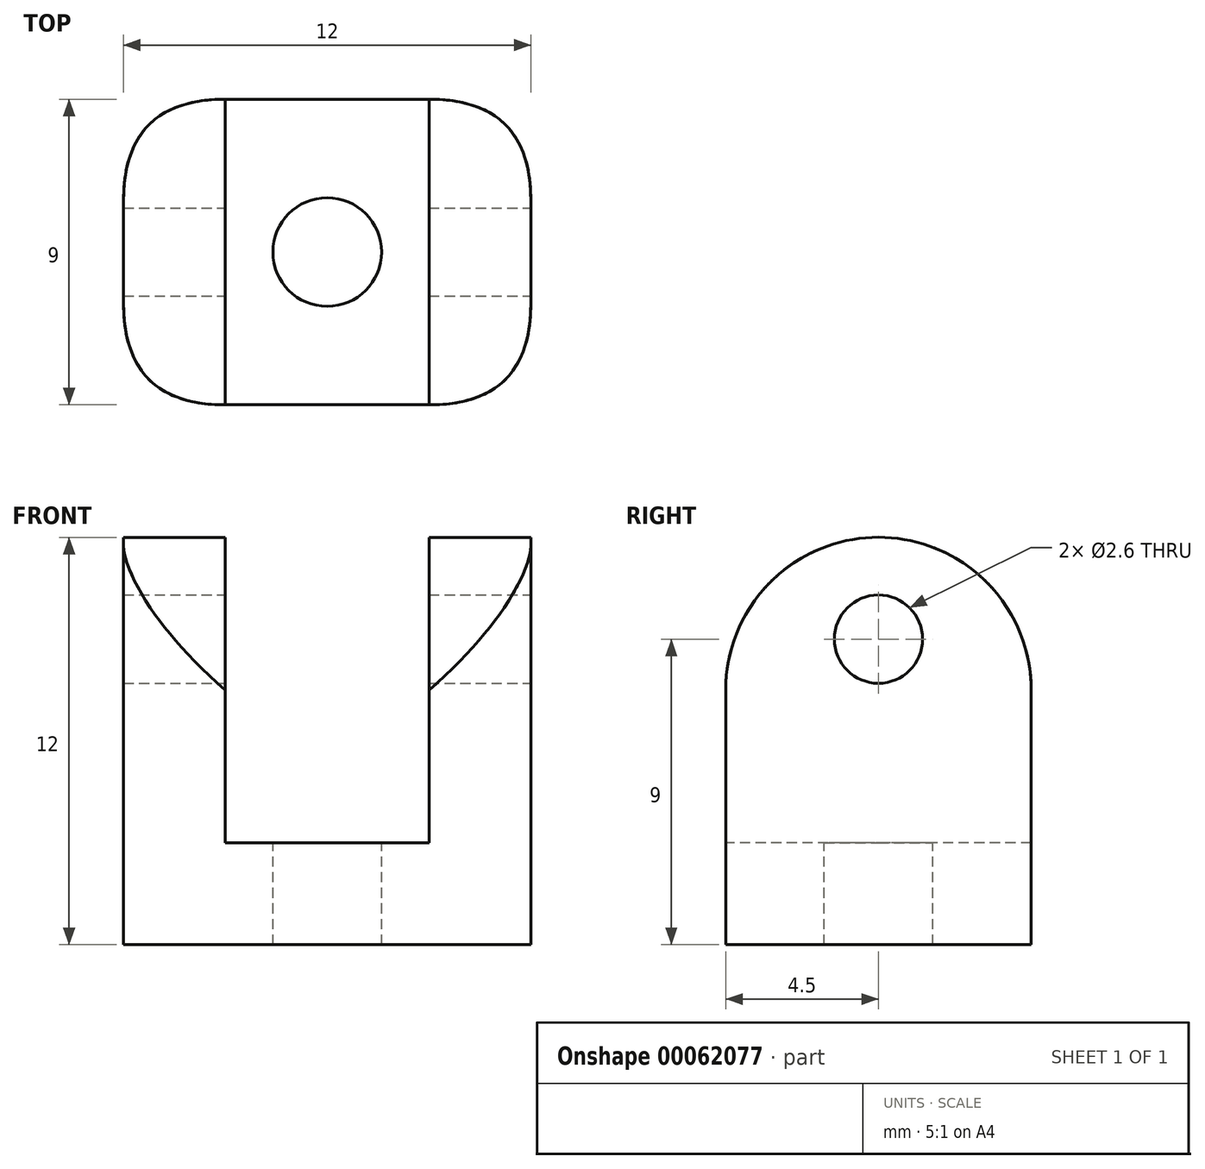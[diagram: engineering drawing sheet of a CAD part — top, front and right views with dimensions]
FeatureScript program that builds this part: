
annotation { "Feature Type Name" : "Feature", "Feature Type Description" : "" }
export const myFeature = defineFeature(function(context is Context, id is Id, definition is map)
    precondition{}
    {
        {
            var Q0;
            Q0=qCreatedBy(makeId("Top.planeOp"),FACE);
            var sketch = newSketch(context, id + "F0", { "sketchPlane" : qUnion([Q0])});
            skLineSegment(sketch, "E0.rect.bottom", {"start": v(6, -4.5) * mm, "end": v(-6, -4.5) * mm});
            skLineSegment(sketch, "E0.rect.top", {"start": v(6, 4.5) * mm, "end": v(-6, 4.5) * mm});
            skLineSegment(sketch, "E0.rect.left", {"start": v(6, -4.5) * mm, "end": v(6, 4.5) * mm});
            skLineSegment(sketch, "E0.rect.right", {"start": v(-6, -4.5) * mm, "end": v(-6, 4.5) * mm});
            skPoint(sketch, "E0.rect.middle", {"position": v(0, 0) * mm});
            skSolve(sketch);
        }
        {
            var Q0;
            Q0=makeQuery(id+"F0.imprint","IMPRINT",FACE,{"disambiguationData":[TD([[makeQuery(id+"F0.imprint","IMPRINT",EDGE,{"derivedFrom":sQuery(id+"F0.wireOp",EDGE,"E0.rect.bottom")}),-1.0]])]});
            var Q1;
            Q1 = qSketchRegion(id + "F4", true);
            extrude(context, id + "F1", {"entities" : qUnion([Q0, Q1]), "depth" : 3 * mm});
        }
        {
            var Q0;
            Q0=makeQuery(id+"F1.opExtrude","CAP_FACE",FACE,{"disambiguationData":[OSD([sQuery(id+"F0.wireOp",EDGE,"E0.rect.bottom"),sQuery(id+"F0.wireOp",EDGE,"E0.rect.top"),sQuery(id+"F0.wireOp",EDGE,"E0.rect.left"),sQuery(id+"F0.wireOp",EDGE,"E0.rect.right")])],"isStart":false});
            var sketch = newSketch(context, id + "F2", { "sketchPlane" : qUnion([Q0])});
            skLineSegment(sketch, "E1", {"start": v(-3, 4.5) * mm, "end": v(-3, -4.5) * mm});
            skLineSegment(sketch, "E2", {"start": v(3, 4.5) * mm, "end": v(3, -4.5) * mm});
            skSolve(sketch);
        }
        {
            var Q0;
            Q0 = qSketchRegion(id + "F2", true);
            var Q1;
            {var subQ0=sQuery(id+"F2.wireOp",EDGE,"E1");Q1=makeQuery(id+"F2.imprint","IMPRINT",FACE,{"disambiguationData":[TD([[makeQuery(id+"F2.imprint","IMPRINT",EDGE,{"derivedFrom":subQ0}),-1.0]])]});}
            var Q2;
            {var subQ0=sQuery(id+"F2.wireOp",EDGE,"E2");Q2=makeQuery(id+"F2.imprint","IMPRINT",FACE,{"disambiguationData":[TD([[makeQuery(id+"F2.imprint","IMPRINT",EDGE,{"derivedFrom":subQ0}),1.0]])]});}
            extrude(context, id + "F3", {"entities" : qUnion([Q0, Q1, Q2]), "operationType" : NewBodyOperationType.ADD, "depth" : 9 * mm});
        }
        {
            var Q0;
            Q0=makeQuery(id+"F1.opExtrude","CAP_FACE",FACE,{"disambiguationData":[OSD([sQuery(id+"F0.wireOp",EDGE,"E0.rect.bottom"),sQuery(id+"F0.wireOp",EDGE,"E0.rect.top"),sQuery(id+"F0.wireOp",EDGE,"E0.rect.left"),sQuery(id+"F0.wireOp",EDGE,"E0.rect.right")])],"isStart":false});
            var sketch = newSketch(context, id + "F4", { "sketchPlane" : qUnion([Q0])});
            skCircle(sketch, "E3", {"center": v(0, 0) * mm, "radius": 1.6 * mm});
            skSolve(sketch);
        }
        {
            var Q0;
            Q0=sQuery(id+"F4.wireOp",VERTEX,"E3.center");
            var Q1;
            Q1=makeQuery(id+"F1.opExtrude","SWEPT_BODY",BODY,{"disambiguationData":[OSD([sQuery(id+"F0.wireOp",EDGE,"E0.rect.bottom"),sQuery(id+"F0.wireOp",EDGE,"E0.rect.top"),sQuery(id+"F0.wireOp",EDGE,"E0.rect.left"),sQuery(id+"F0.wireOp",EDGE,"E0.rect.right")])]});
            hole(context, id + "F5", {"style" : HoleStyle.SIMPLE, "holeDiameter" : 3.2 * mm, "endStyle" : HoleEndStyle.THROUGH, "locations" : qUnion([Q0]), "scope" : qUnion([Q1])});
        }
        {
            var Q0;
            {var subQ0=sQuery(id+"F0.wireOp",EDGE,"E0.rect.left");Q0=makeQuery(id+"F3.boolean.opBoolean","MERGE",FACE,{"derivedFrom":[makeQuery(id+"F1.opExtrude","SWEPT_FACE",FACE,{"disambiguationData":[OSD([subQ0])]}),makeQuery(id+"F3.opExtrude","SWEPT_FACE",FACE,{"disambiguationData":[OSD([subQ0])]})]});}
            var sketch = newSketch(context, id + "F6", { "sketchPlane" : qUnion([Q0])});
            skCircle(sketch, "E4", {"center": v(0, 9) * mm, "radius": 1.6 * mm});
            skSolve(sketch);
        }
        {
            var Q0;
            Q0=sQuery(id+"F6.wireOp",VERTEX,"E4.center");
            var Q1;
            Q1=makeQuery(id+"F1.opExtrude","SWEPT_BODY",BODY,{"disambiguationData":[OSD([sQuery(id+"F0.wireOp",EDGE,"E0.rect.bottom"),sQuery(id+"F0.wireOp",EDGE,"E0.rect.top"),sQuery(id+"F0.wireOp",EDGE,"E0.rect.left"),sQuery(id+"F0.wireOp",EDGE,"E0.rect.right")])]});
            hole(context, id + "F7", {"style" : HoleStyle.SIMPLE, "holeDiameter" : 2.6 * mm, "endStyle" : HoleEndStyle.THROUGH, "locations" : qUnion([Q0]), "scope" : qUnion([Q1])});
        }
        {
            var Q0;
            {var subQ0=sQuery(id+"F0.wireOp",EDGE,"E0.rect.top");var subQ1=makeQuery(id+"F1.opExtrude","CAP_EDGE",EDGE,{"disambiguationData":[OSD([subQ0])],"isStart":false});Q0=makeQuery(id+"F3.opExtrude","CAP_EDGE",EDGE,{"disambiguationData":[OSD([subQ0]),TDD([makeQuery(id+"F2.imprint","IMPRINT",EDGE,{"disambiguationData":[TD([[makeQuery(id+"F2.imprint","INTERSECT",VERTEX,{"derivedFrom":[subQ1,makeQuery(id+"F1.opExtrude","CAP_EDGE",EDGE,{"disambiguationData":[OSD([sQuery(id+"F0.wireOp",EDGE,"E0.rect.right")])],"isStart":false})]}),1.0]])],"derivedFrom":subQ1})])],"isStart":false});}
            var Q1;
            {var subQ0=sQuery(id+"F0.wireOp",EDGE,"E0.rect.top");var subQ1=makeQuery(id+"F1.opExtrude","CAP_EDGE",EDGE,{"disambiguationData":[OSD([subQ0])],"isStart":false});Q1=makeQuery(id+"F3.opExtrude","CAP_EDGE",EDGE,{"disambiguationData":[OSD([subQ0]),TDD([makeQuery(id+"F2.imprint","IMPRINT",EDGE,{"disambiguationData":[TD([[makeQuery(id+"F2.imprint","INTERSECT",VERTEX,{"derivedFrom":[subQ1,makeQuery(id+"F1.opExtrude","CAP_EDGE",EDGE,{"disambiguationData":[OSD([sQuery(id+"F0.wireOp",EDGE,"E0.rect.left")])],"isStart":false})]}),-1.0]])],"derivedFrom":subQ1})])],"isStart":false});}
            var Q2;
            {var subQ0=sQuery(id+"F0.wireOp",EDGE,"E0.rect.bottom");var subQ1=makeQuery(id+"F1.opExtrude","CAP_EDGE",EDGE,{"disambiguationData":[OSD([subQ0])],"isStart":false});Q2=makeQuery(id+"F3.opExtrude","CAP_EDGE",EDGE,{"disambiguationData":[OSD([subQ0]),TDD([makeQuery(id+"F2.imprint","IMPRINT",EDGE,{"disambiguationData":[TD([[makeQuery(id+"F2.imprint","INTERSECT",VERTEX,{"derivedFrom":[subQ1,makeQuery(id+"F1.opExtrude","CAP_EDGE",EDGE,{"disambiguationData":[OSD([sQuery(id+"F0.wireOp",EDGE,"E0.rect.right")])],"isStart":false})]}),1.0]])],"derivedFrom":subQ1})])],"isStart":false});}
            var Q3;
            {var subQ0=sQuery(id+"F0.wireOp",EDGE,"E0.rect.bottom");var subQ1=makeQuery(id+"F1.opExtrude","CAP_EDGE",EDGE,{"disambiguationData":[OSD([subQ0])],"isStart":false});Q3=makeQuery(id+"F3.opExtrude","CAP_EDGE",EDGE,{"disambiguationData":[OSD([subQ0]),TDD([makeQuery(id+"F2.imprint","IMPRINT",EDGE,{"disambiguationData":[TD([[makeQuery(id+"F2.imprint","INTERSECT",VERTEX,{"derivedFrom":[subQ1,makeQuery(id+"F1.opExtrude","CAP_EDGE",EDGE,{"disambiguationData":[OSD([sQuery(id+"F0.wireOp",EDGE,"E0.rect.left")])],"isStart":false})]}),-1.0]])],"derivedFrom":subQ1})])],"isStart":false});}
            fillet(context, id + "F8", {"entities" : qUnion([Q0, Q1, Q2, Q3]), "radius" : 4.5 * mm, "tangentPropagation" : true, "allowEdgeOverflow" : false});
        }
        {
            var Q0;
            {var subQ0=sQuery(id+"F0.wireOp",EDGE,"E0.rect.right");var subQ1=sQuery(id+"F0.wireOp",EDGE,"E0.rect.bottom");Q0=makeQuery(id+"F3.boolean.opBoolean","MERGE",EDGE,{"derivedFrom":[makeQuery(id+"F1.opExtrude","SWEPT_EDGE",EDGE,{"disambiguationData":[OSD([subQ1,subQ0])]}),makeQuery(id+"F3.opExtrude","SWEPT_EDGE",EDGE,{"disambiguationData":[OSD([subQ1,subQ0])]})]});}
            var Q1;
            {var subQ0=sQuery(id+"F0.wireOp",EDGE,"E0.rect.right");var subQ1=sQuery(id+"F0.wireOp",EDGE,"E0.rect.top");Q1=makeQuery(id+"F3.boolean.opBoolean","MERGE",EDGE,{"derivedFrom":[makeQuery(id+"F1.opExtrude","SWEPT_EDGE",EDGE,{"disambiguationData":[OSD([subQ1,subQ0])]}),makeQuery(id+"F3.opExtrude","SWEPT_EDGE",EDGE,{"disambiguationData":[OSD([subQ1,subQ0])]})]});}
            var Q2;
            {var subQ0=sQuery(id+"F0.wireOp",EDGE,"E0.rect.left");var subQ1=sQuery(id+"F0.wireOp",EDGE,"E0.rect.bottom");Q2=makeQuery(id+"F3.boolean.opBoolean","MERGE",EDGE,{"derivedFrom":[makeQuery(id+"F1.opExtrude","SWEPT_EDGE",EDGE,{"disambiguationData":[OSD([subQ1,subQ0])]}),makeQuery(id+"F3.opExtrude","SWEPT_EDGE",EDGE,{"disambiguationData":[OSD([subQ1,subQ0])]})]});}
            var Q3;
            {var subQ0=sQuery(id+"F0.wireOp",EDGE,"E0.rect.left");var subQ1=sQuery(id+"F0.wireOp",EDGE,"E0.rect.top");Q3=makeQuery(id+"F3.boolean.opBoolean","MERGE",EDGE,{"derivedFrom":[makeQuery(id+"F1.opExtrude","SWEPT_EDGE",EDGE,{"disambiguationData":[OSD([subQ1,subQ0])]}),makeQuery(id+"F3.opExtrude","SWEPT_EDGE",EDGE,{"disambiguationData":[OSD([subQ1,subQ0])]})]});}
            fillet(context, id + "F9", {"entities" : qUnion([Q0, Q1, Q2, Q3]), "radius" : 3 * mm, "rho" : 0.5, "crossSection" : FilletCrossSection.CONIC, "allowEdgeOverflow" : false});
        }
    });
